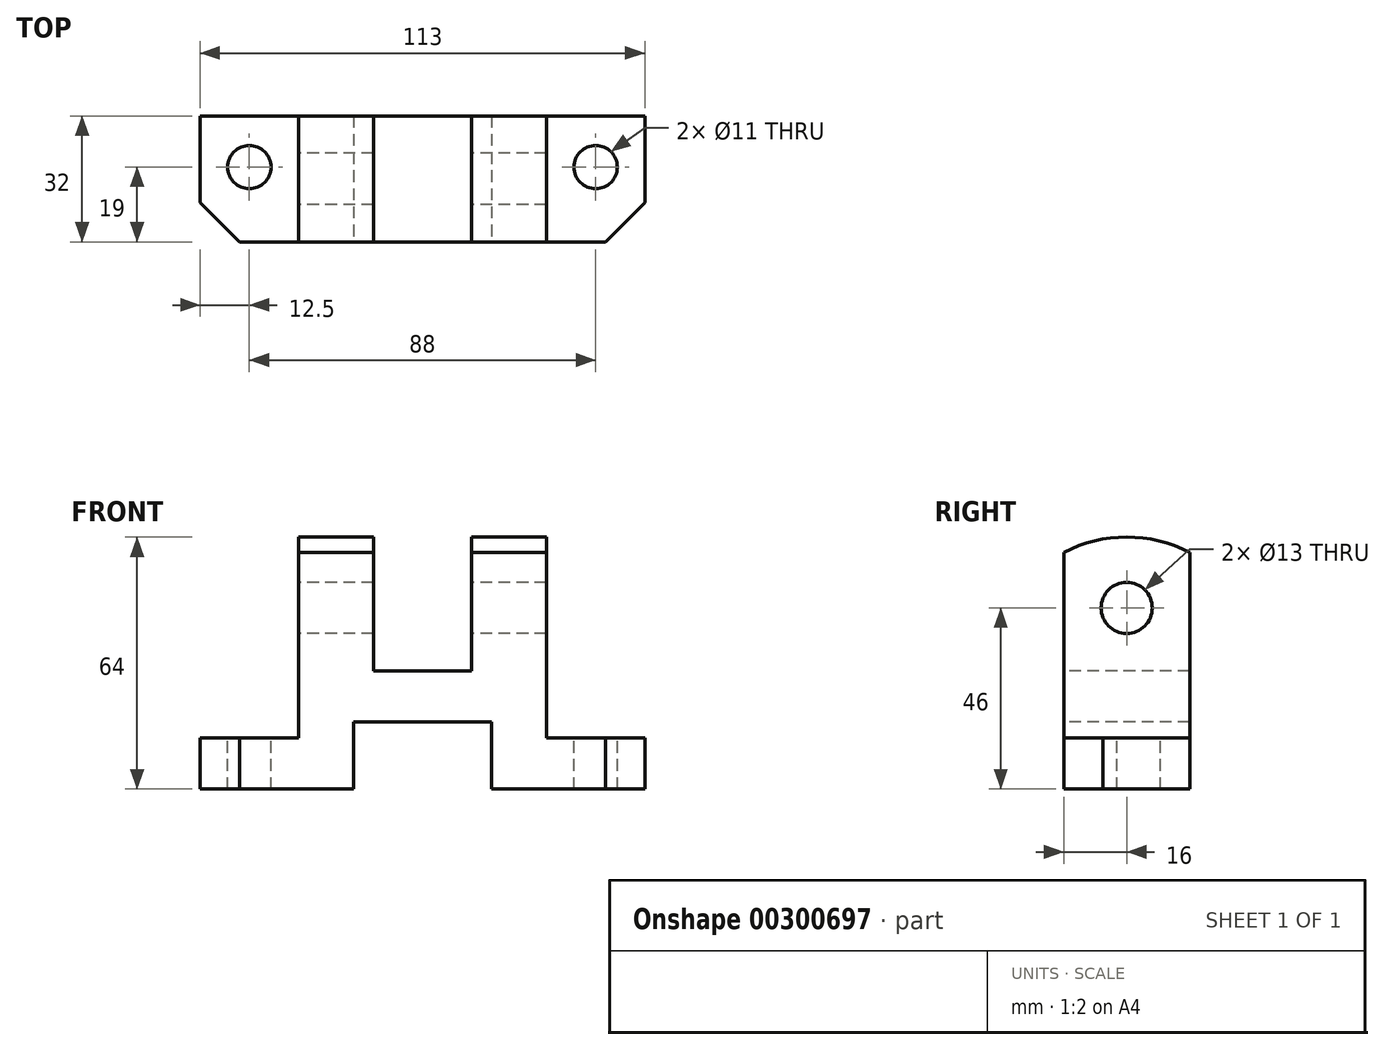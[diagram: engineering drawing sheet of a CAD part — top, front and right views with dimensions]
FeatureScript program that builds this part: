
annotation { "Feature Type Name" : "Feature", "Feature Type Description" : "" }
export const myFeature = defineFeature(function(context is Context, id is Id, definition is map)
    precondition{}
    {
        {
            var Q0;
            Q0=qCreatedBy(makeId("Right.planeOp"),FACE);
            var sketch = newSketch(context, id + "F0", { "sketchPlane" : qUnion([Q0])});
            skLineSegment(sketch, "E0", {"start": v(-32, 60.13) * mm, "end": v(-32, 0) * mm});
            skLineSegment(sketch, "E1", {"start": v(-32, 0) * mm, "end": v(0, 0) * mm});
            skLineSegment(sketch, "E2", {"start": v(0, 0) * mm, "end": v(0, 60.13) * mm});
            skArc(sketch, "E3", {"start": v(0, 60.13) * mm, "mid": v(-16, 64) * mm, "end": v(-32, 60.13) * mm});
            skCircle(sketch, "E4", {"center": v(-16, 46) * mm, "radius": 6.5 * mm});
            skSolve(sketch);
        }
        {
            var Q0;
            Q0 = qSketchRegion(id + "F0", true);
            extrude(context, id + "F1", {"entities" : qUnion([Q0]), "depth" : 113 * mm});
        }
        {
            var Q0;
            Q0=makeQuery(id+"F1.opExtrude","CAP_FACE",FACE,{"disambiguationData":[OSD([sQuery(id+"F0.wireOp",EDGE,"E0"),sQuery(id+"F0.wireOp",EDGE,"E1"),sQuery(id+"F0.wireOp",EDGE,"E2"),sQuery(id+"F0.wireOp",EDGE,"E3"),sQuery(id+"F0.wireOp",EDGE,"E4")])],"isStart":false});
            var sketch = newSketch(context, id + "F2", { "sketchPlane" : qUnion([Q0])});
            skLineSegment(sketch, "E5.bottom", {"start": v(-33, 64) * mm, "end": v(1.95, 64) * mm});
            skLineSegment(sketch, "E5.top", {"start": v(-33, 13) * mm, "end": v(1.95, 13) * mm});
            skLineSegment(sketch, "E5.left", {"start": v(-33, 64) * mm, "end": v(-33, 13) * mm});
            skLineSegment(sketch, "E5.right", {"start": v(1.95, 64) * mm, "end": v(1.95, 13) * mm});
            skPoint(sketch, "E5.middle", {"position": v(-15.52, 38.5) * mm});
            skSolve(sketch);
        }
        {
            var Q0;
            Q0 = qSketchRegion(id + "F2", true);
            extrude(context, id + "F3", {"entities" : qUnion([Q0]), "operationType" : NewBodyOperationType.REMOVE, "oppositeDirection" : true, "depth" : 25 * mm});
        }
        {
            var Q0;
            Q0=makeQuery(id+"F1.opExtrude","CAP_FACE",FACE,{"disambiguationData":[OSD([sQuery(id+"F0.wireOp",EDGE,"E0"),sQuery(id+"F0.wireOp",EDGE,"E1"),sQuery(id+"F0.wireOp",EDGE,"E2"),sQuery(id+"F0.wireOp",EDGE,"E3"),sQuery(id+"F0.wireOp",EDGE,"E4")])],"isStart":true});
            var sketch = newSketch(context, id + "F4", { "sketchPlane" : qUnion([Q0])});
            skLineSegment(sketch, "E6.bottom", {"start": v(-32.04, 64) * mm, "end": v(65.25, 64) * mm});
            skLineSegment(sketch, "E6.top", {"start": v(-32.04, 13) * mm, "end": v(65.25, 13) * mm});
            skLineSegment(sketch, "E6.left", {"start": v(-32.04, 64) * mm, "end": v(-32.04, 13) * mm});
            skLineSegment(sketch, "E6.right", {"start": v(65.25, 64) * mm, "end": v(65.25, 13) * mm});
            skPoint(sketch, "E6.middle", {"position": v(16.6, 38.5) * mm});
            skSolve(sketch);
        }
        {
            var Q0;
            Q0 = qSketchRegion(id + "F4", true);
            extrude(context, id + "F5", {"entities" : qUnion([Q0]), "operationType" : NewBodyOperationType.REMOVE, "oppositeDirection" : true, "depth" : 25 * mm});
        }
        {
            var Q0;
            Q0=makeQuery(id+"F1.opExtrude","SWEPT_FACE",FACE,{"disambiguationData":[OSD([sQuery(id+"F0.wireOp",EDGE,"E0")])]});
            var sketch = newSketch(context, id + "F6", { "sketchPlane" : qUnion([Q0])});
            skLineSegment(sketch, "E7", {"start": v(39, 0) * mm, "end": v(39, 17) * mm});
            skLineSegment(sketch, "E8", {"start": v(39, 17) * mm, "end": v(74, 17) * mm});
            skLineSegment(sketch, "E9", {"start": v(74, 17) * mm, "end": v(74, 0) * mm});
            skLineSegment(sketch, "E10", {"start": v(74, 0) * mm, "end": v(39, 0) * mm});
            skLineSegment(sketch, "E11.bottom", {"start": v(69, 30) * mm, "end": v(44, 30) * mm});
            skLineSegment(sketch, "E11.top", {"start": v(69, 64.34) * mm, "end": v(44, 64.34) * mm});
            skLineSegment(sketch, "E11.left", {"start": v(69, 30) * mm, "end": v(69, 64.34) * mm});
            skLineSegment(sketch, "E11.right", {"start": v(44, 30) * mm, "end": v(44, 64.34) * mm});
            skPoint(sketch, "E11.middle", {"position": v(56.5, 47.17) * mm});
            skSolve(sketch);
        }
        {
            var Q0;
            Q0=makeQuery(id+"F3.boolean.opBoolean","COPY",FACE,{"derivedFrom":makeQuery(id+"F3.opExtrude","SWEPT_FACE",FACE,{"disambiguationData":[OSD([sQuery(id+"F2.wireOp",EDGE,"E5.top")])]})});
            var sketch = newSketch(context, id + "F7", { "sketchPlane" : qUnion([Q0])});
            skCircle(sketch, "E12", {"center": v(100.5, -13) * mm, "radius": 5.5 * mm});
            skCircle(sketch, "E13", {"center": v(12.5, -13) * mm, "radius": 5.5 * mm});
            skLineSegment(sketch, "E14", {"start": v(113, -27.06) * mm, "end": v(108.06, -32) * mm});
            skLineSegment(sketch, "E15", {"start": v(0, -27.43) * mm, "end": v(4.28, -31.71) * mm});
            skSolve(sketch);
        }
        {
            var Q0;
            Q0 = qSketchRegion(id + "F7", true);
            extrude(context, id + "F8", {"entities" : qUnion([Q0]), "operationType" : NewBodyOperationType.REMOVE, "oppositeDirection" : true, "depth" : 25 * mm});
        }
        {
            var Q0;
            Q0 = qSketchRegion(id + "F6", true);
            extrude(context, id + "F9", {"entities" : qUnion([Q0]), "operationType" : NewBodyOperationType.REMOVE, "endBound" : BoundingType.THROUGH_ALL, "oppositeDirection" : true, "depth" : 25 * mm});
        }
        {
            var Q0;
            Q0=makeQuery(id+"F5.boolean.opBoolean","COPY",FACE,{"derivedFrom":makeQuery(id+"F5.opExtrude","SWEPT_FACE",FACE,{"disambiguationData":[OSD([sQuery(id+"F4.wireOp",EDGE,"E6.top")])]})});
            var sketch = newSketch(context, id + "F10", { "sketchPlane" : qUnion([Q0])});
            skLineSegment(sketch, "E16", {"start": v(0, -32) * mm, "end": v(0, -22) * mm});
            skLineSegment(sketch, "E17", {"start": v(0, -22) * mm, "end": v(10, -32) * mm});
            skLineSegment(sketch, "E18", {"start": v(10, -32) * mm, "end": v(0, -32) * mm});
            skSolve(sketch);
        }
        {
            var Q0;
            Q0 = qSketchRegion(id + "F10", true);
            extrude(context, id + "F11", {"entities" : qUnion([Q0]), "operationType" : NewBodyOperationType.REMOVE, "oppositeDirection" : true, "depth" : 25 * mm});
        }
        {
            var Q0;
            Q0=makeQuery(id+"F3.boolean.opBoolean","COPY",FACE,{"derivedFrom":makeQuery(id+"F3.opExtrude","SWEPT_FACE",FACE,{"disambiguationData":[OSD([sQuery(id+"F2.wireOp",EDGE,"E5.top")])]})});
            var sketch = newSketch(context, id + "F12", { "sketchPlane" : qUnion([Q0])});
            skLineSegment(sketch, "E19", {"start": v(113, -32) * mm, "end": v(103, -32) * mm});
            skLineSegment(sketch, "E20", {"start": v(103, -32) * mm, "end": v(113, -22) * mm});
            skLineSegment(sketch, "E21", {"start": v(113, -22) * mm, "end": v(113, -32) * mm});
            skSolve(sketch);
        }
        {
            var Q0;
            Q0 = qSketchRegion(id + "F12", true);
            extrude(context, id + "F13", {"entities" : qUnion([Q0]), "operationType" : NewBodyOperationType.REMOVE, "oppositeDirection" : true, "depth" : 25 * mm});
        }
    });
